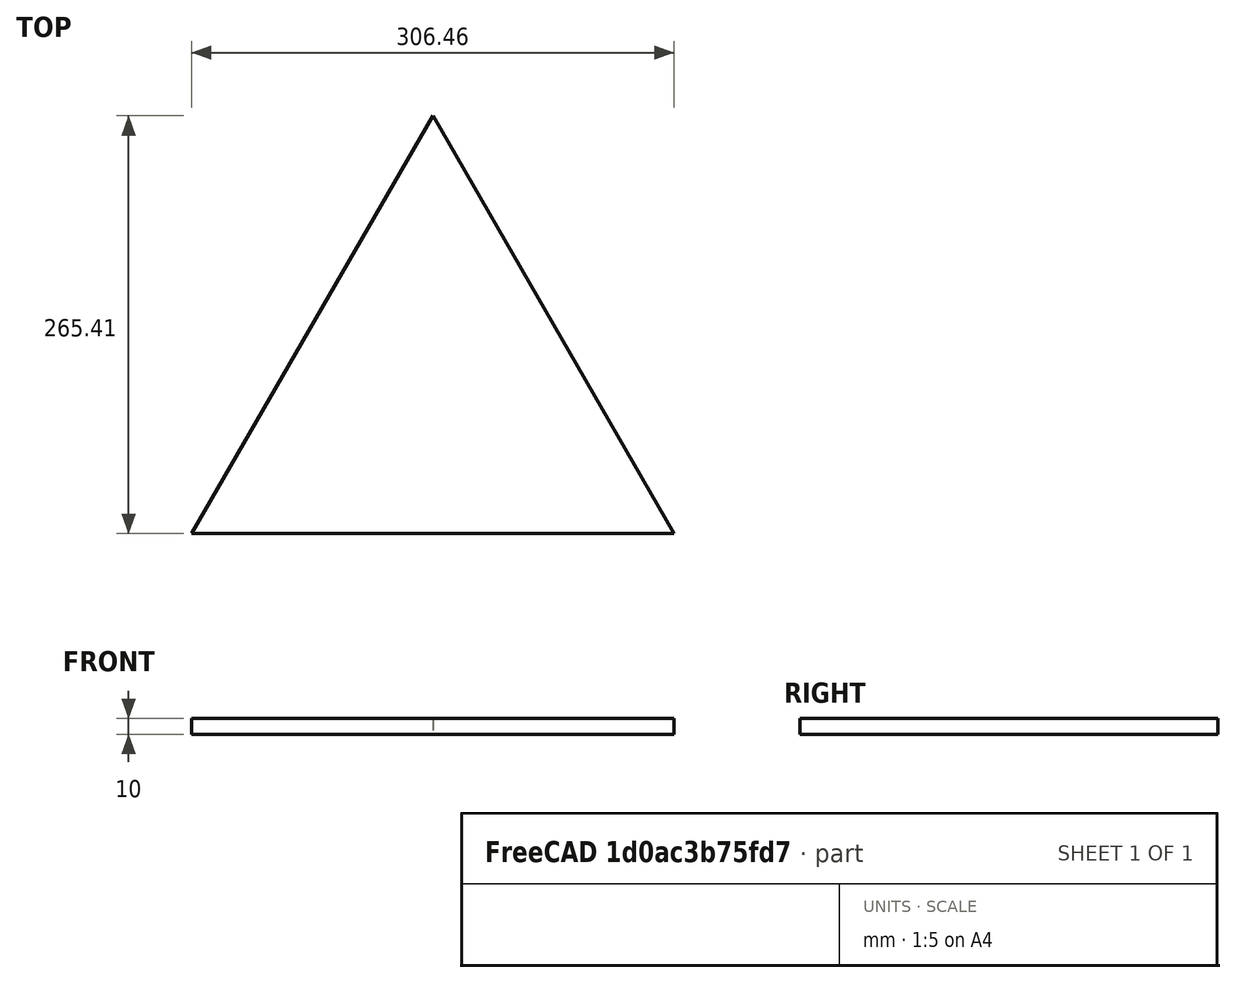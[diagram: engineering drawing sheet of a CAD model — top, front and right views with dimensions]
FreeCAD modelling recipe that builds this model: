
FCSTD DOCUMENT  (FreeCAD 0.19R)
Label: Model Triangle
License: All rights reserved
LicenseURL: http://en.wikipedia.org/wiki/All_rights_reserved
objects: Sketcher::SketchObject×1, PartDesign::Pad×1, PartDesign::Body×1
note: 4 computed .brp shape members not serialized (recipe doc carries the construction recipe); baked Part::Feature solids carry a one-line shape summary decoded from their .brp

FEATURE [Sketcher::SketchObject] Sketch011  label="Board"
  FullyConstrained = false
  MapMode = 5
  Support = -> [XY_Plane011]
  sketch-geometry (4):
    g0: LineSegment StartX=-47.2056 StartY=137.74 StartZ=0 EndX=-200.437 EndY=-127.665 EndZ=0
    g1: LineSegment StartX=-200.437 StartY=-127.665 StartZ=0 EndX=106.026 EndY=-127.665 EndZ=0
    g2: LineSegment StartX=106.026 StartY=-127.665 StartZ=0 EndX=-47.2056 EndY=137.74 EndZ=0
    g3: Circle CenterX=-47.2056 CenterY=-39.1968 CenterZ=0 NormalX=0 NormalY=0 NormalZ=1 AngleXU=0 Radius=176.937
  constraints (8):
    c: Coincident(g0,g1)
    c: Coincident(g1,g2)
    c: Coincident(g2,g0)
    c: Equal(g0,g1)
    c: Equal(g0,g2)
    c: PointOnObject(g0,g3)
    c: PointOnObject(g1,g3)
    c: PointOnObject(g2,g3)
FEATURE [PartDesign::Pad] Pad011
  Direction = (1,1,1)
  Length = 10
  Length2 = 100
  Profile = -> Sketch011
  Reversed = true
  Type = 0
FEATURE [PartDesign::Body] Body011  label="Board Body"
  Group = -> [Sketch011,Pad011]
  Origin = -> Origin011
  Placement = pos=(200.437,127.665,0) rot=(0,0,1;0rad)
  Tip = -> Pad011
